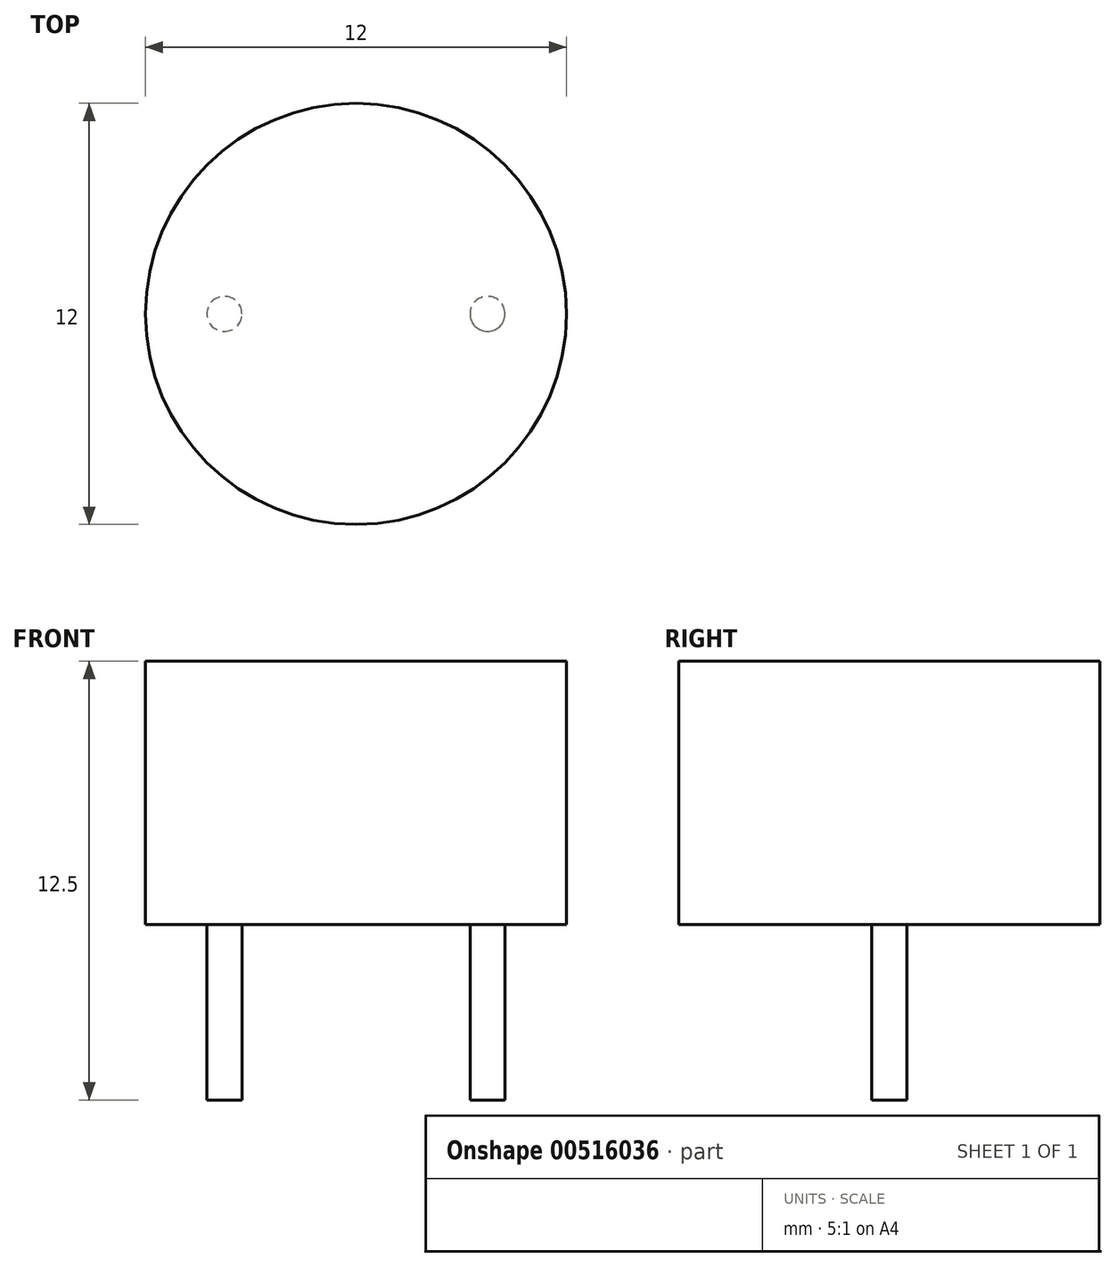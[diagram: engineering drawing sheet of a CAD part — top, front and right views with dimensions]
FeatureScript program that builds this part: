
annotation { "Feature Type Name" : "Feature", "Feature Type Description" : "" }
export const myFeature = defineFeature(function(context is Context, id is Id, definition is map)
    precondition{}
    {
        {
            var Q0;
            Q0=qCreatedBy(makeId("Top.planeOp"),FACE);
            var sketch = newSketch(context, id + "F0", { "sketchPlane" : qUnion([Q0])});
            skCircle(sketch, "E0", {"center": v(0, 0) * mm, "radius": 6 * mm});
            skSolve(sketch);
        }
        {
            var Q0;
            Q0 = qSketchRegion(id + "F0", true);
            extrude(context, id + "F1", {"entities" : qUnion([Q0]), "depth" : 7.5 * mm, "offsetDistance" : 25 * mm});
        }
        {
            var Q0;
            Q0=makeQuery(id+"F1.opExtrude","CAP_FACE",FACE,{"disambiguationData":[OSD([sQuery(id+"F0.wireOp",EDGE,"E0")])],"isStart":true});
            var sketch = newSketch(context, id + "F2", { "sketchPlane" : qUnion([Q0])});
            skCircle(sketch, "E1", {"center": v(-3.75, 0) * mm, "radius": 0.5 * mm});
            skCircle(sketch, "E2", {"center": v(3.75, 0) * mm, "radius": 0.5 * mm});
            skSolve(sketch);
        }
        {
            var Q0;
            Q0 = qSketchRegion(id + "F2", true);
            extrude(context, id + "F3", {"entities" : qUnion([Q0]), "operationType" : NewBodyOperationType.ADD, "depth" : 5 * mm, "offsetDistance" : 25 * mm});
        }
    });
